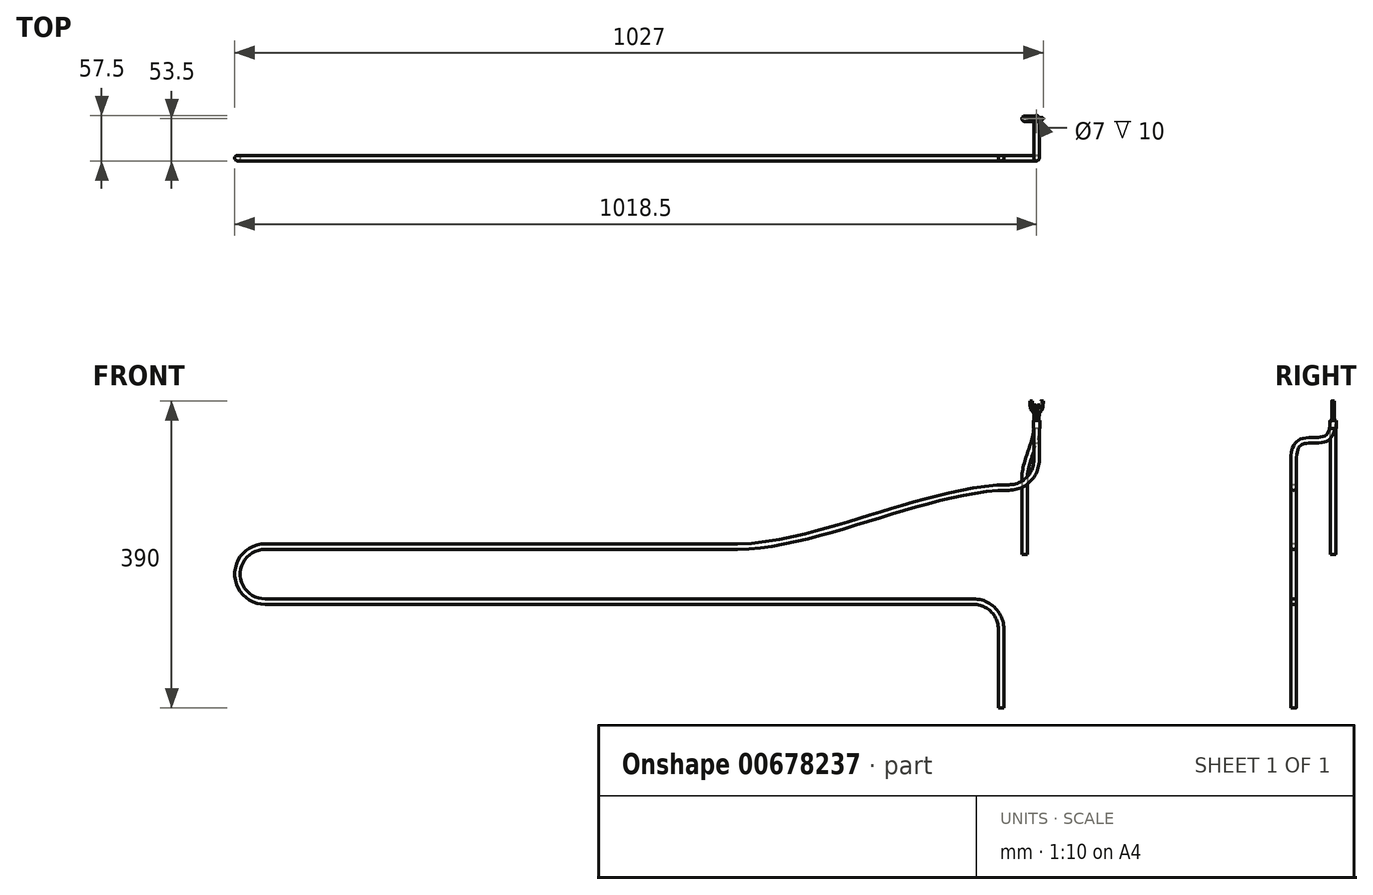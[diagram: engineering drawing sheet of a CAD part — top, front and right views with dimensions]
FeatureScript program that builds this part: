
annotation { "Feature Type Name" : "Feature", "Feature Type Description" : "" }
export const myFeature = defineFeature(function(context is Context, id is Id, definition is map)
    precondition{}
    {
        {
            var Q0;
            Q0=qCreatedBy(makeId("Top.planeOp"),FACE);
            var sketch = newSketch(context, id + "F0", { "sketchPlane" : qUnion([Q0])});
            skCircle(sketch, "E0", {"center": v(0, 0) * mm, "radius": 3.5 * mm});
            skSolve(sketch);
        }
        {
            var Q0;
            Q0=qCreatedBy(makeId("Front.planeOp"),FACE);
            var sketch = newSketch(context, id + "F1", { "sketchPlane" : qUnion([Q0])});
            skLineSegment(sketch, "E1", {"start": v(0, 0) * mm, "end": v(0, -10) * mm});
            skFitSpline(sketch, "E2", {"points": [v(0, -10) * mm, v(-15, -70) * mm], "startDerivative": vector(0, -45) * mm, "endDerivative": vector(0, -45) * mm});
            skLineSegment(sketch, "E3", {"start": v(-15, -70) * mm, "end": v(-15, -170) * mm});
            skSolve(sketch);
        }
        {
            var Q0;
            Q0=qSketchRegion(id+"F0",true);
            var Q1;
            Q1=qConstructionFilter(qBodyType(qCreatedBy(id+"F1",EDGE),BodyType.WIRE),ConstructionObject.NO);
            sweep(context, id + "F2", {"profiles" : qUnion([Q0]), "path" : qUnion([Q1])});
        }
        {
            var Q0;
            Q0=makeQuery(id+"F2.opSweep","CAP_FACE",FACE,{"disambiguationData":[OSD([sQuery(id+"F0.wireOp",EDGE,"E0"),sQuery(id+"F1.wireOp",VERTEX,"E1.start")])],"isStart":true});
            var sketch = newSketch(context, id + "F3", { "sketchPlane" : qUnion([Q0])});
            skCircle(sketch, "E4", {"center": v(1.5, 0) * mm, "radius": 1.5 * mm});
            skSolve(sketch);
        }
        {
            var Q0;
            Q0=qCreatedBy(makeId("Front.planeOp"),FACE);
            var sketch = newSketch(context, id + "F4", { "sketchPlane" : qUnion([Q0])});
            skFitSpline(sketch, "E5", {"points": [v(1.5, 0) * mm, v(2.5, 15) * mm], "startDerivative": vector(0, 15) * mm, "endDerivative": vector(0, 15) * mm});
            skLineSegment(sketch, "E6", {"start": v(2.5, 15) * mm, "end": v(2.5, 20) * mm});
            skSolve(sketch);
        }
        {
            var Q0;
            Q0=qSketchRegion(id+"F3",true);
            var Q1;
            Q1=qConstructionFilter(qBodyType(qCreatedBy(id+"F4",EDGE),BodyType.WIRE),ConstructionObject.NO);
            sweep(context, id + "F5", {"profiles" : qUnion([Q0]), "path" : qUnion([Q1])});
        }
        {
            var Q0;
            Q0=makeQuery(id+"F5.opSweep","SWEPT_BODY",BODY,{"disambiguationData":[OSD([sQuery(id+"F3.wireOp",EDGE,"E4"),sQuery(id+"F4.wireOp",EDGE,"E6")])]});
            var Q1;
            Q1=qCreatedBy(makeId("Right.planeOp"),FACE);
            mirror(context, id + "F6", {"entities" : qUnion([Q0]), "mirrorPlane" : qUnion([Q1])});
        }
        {
            var Q0;
            Q0=makeQuery(id+"F2.opSweep","CAP_FACE",FACE,{"disambiguationData":[OSD([sQuery(id+"F0.wireOp",EDGE,"E0"),sQuery(id+"F1.wireOp",VERTEX,"E1.start")])],"isStart":true});
            var sketch = newSketch(context, id + "F7", { "sketchPlane" : qUnion([Q0])});
            skCircle(sketch, "E7.0", {"center": v(0, 0) * mm, "radius": 3.5 * mm});
            skCircle(sketch, "E8.0", {"center": v(0, 0) * mm, "radius": 4 * mm});
            skSolve(sketch);
        }
        {
            var Q0;
            Q0=qSketchRegion(id+"F7",true);
            extrude(context, id + "F8", {"entities" : qUnion([Q0]), "oppositeDirection" : true, "depth" : 10 * mm, "offsetDistance" : 25 * mm});
        }
        {
            var Q0;
            Q0=qCreatedBy(makeId("Front.planeOp"),FACE);
            var sketch = newSketch(context, id + "F9", { "sketchPlane" : qUnion([Q0])});
            skFitSpline(sketch, "E9", {"points": [v(1.5, 0) * mm, v(4.25, 12.5) * mm, v(7, 25) * mm], "startDerivative": vector(0, 60) * mm, "endDerivative": vector(0, 60) * mm});
            skLineSegment(sketch, "E10", {"start": v(1.5, 10) * mm, "end": v(1.5, 0) * mm, "construction": true});
            skLineSegment(sketch, "E11", {"start": v(7, 25) * mm, "end": v(7, 15) * mm, "construction": true});
            skLineSegment(sketch, "E12", {"start": v(1.5, 0) * mm, "end": v(7, 25) * mm, "construction": true});
            skSolve(sketch);
        }
        {
            var Q0;
            Q0=qSketchRegion(id+"F3",true);
            var Q1;
            Q1=sQuery(id+"F9.wireOp",EDGE,"E9");
            sweep(context, id + "F10", {"profiles" : qUnion([Q0]), "path" : qUnion([Q1])});
        }
        {
            var Q0;
            Q0=makeQuery(id+"F10.opSweep","SWEPT_BODY",BODY,{"disambiguationData":[OSD([sQuery(id+"F3.wireOp",EDGE,"E4"),sQuery(id+"F9.wireOp",EDGE,"E9")])]});
            var Q1;
            Q1=qCreatedBy(makeId("Right.planeOp"),FACE);
            mirror(context, id + "F11", {"entities" : qUnion([Q0]), "mirrorPlane" : qUnion([Q1])});
        }
        {
            var Q0;
            Q0=qCreatedBy(makeId("Right.planeOp"),FACE);
            var sketch = newSketch(context, id + "F12", { "sketchPlane" : qUnion([Q0])});
            skFitSpline(sketch, "E13", {"points": [v(0, 0) * mm, v(-25, -25) * mm, v(-50, -50) * mm], "startDerivative": vector(0, -150) * mm, "endDerivative": vector(0, -150) * mm});
            skLineSegment(sketch, "E14", {"start": v(-50, -25) * mm, "end": v(-50, -50) * mm, "construction": true});
            skLineSegment(sketch, "E15", {"start": v(0, -25) * mm, "end": v(0, 0) * mm, "construction": true});
            skLineSegment(sketch, "E16", {"start": v(0, 0) * mm, "end": v(-50, -50) * mm, "construction": true});
            skSolve(sketch);
        }
        {
            var Q0;
            Q0=qCreatedBy(makeId("Front.planeOp"),FACE);
            var Q1;
            Q1=sQuery(id+"F12.wireOp",VERTEX,"E13.2.internal");
            cPlane(context, id + "F13", {"entities" : qUnion([Q0, Q1]), "cplaneType" : CPlaneType.PLANE_POINT, "offset" : 25 * mm, "width" : 150 * mm, "height" : 150 * mm});
        }
        {
            var Q0;
            Q0=qCreatedBy(id+"F13.planeOp",FACE);
            var sketch = newSketch(context, id + "F14", { "sketchPlane" : qUnion([Q0])});
            skLineSegment(sketch, "E17", {"start": v(-380, -160) * mm, "end": v(-980, -160) * mm});
            skArc(sketch, "E18", {"start": v(-980, -160) * mm, "mid": v(-1015, -195) * mm, "end": v(-980, -230) * mm});
            skLineSegment(sketch, "E19", {"start": v(-980, -230) * mm, "end": v(-80, -230) * mm});
            skArc(sketch, "E20", {"start": v(-45, -265) * mm, "mid": v(-55.25, -240.25) * mm, "end": v(-80, -230) * mm});
            skLineSegment(sketch, "E21", {"start": v(-45, -265) * mm, "end": v(-45, -365) * mm});
            skArc(sketch, "E22", {"start": v(-35, -85) * mm, "mid": v(-10.25, -74.75) * mm, "end": v(0, -50) * mm});
            skFitSpline(sketch, "E23", {"points": [v(-380, -160) * mm, v(-207.5, -122.5) * mm, v(-35, -85) * mm], "startDerivative": vector(300, 0) * mm, "endDerivative": vector(300, 0) * mm});
            skLineSegment(sketch, "E24", {"start": v(-85, -85) * mm, "end": v(-35, -85) * mm, "construction": true});
            skLineSegment(sketch, "E25", {"start": v(-330, -160) * mm, "end": v(-380, -160) * mm, "construction": true});
            skLineSegment(sketch, "E26", {"start": v(-380, -160) * mm, "end": v(-35, -85) * mm, "construction": true});
            skSolve(sketch);
        }
        {
            var Q0;
            Q0=qSketchRegion(id+"F0",true);
            var Q1;
            Q1=sQuery(id+"F12.wireOp",EDGE,"E13");
            var Q2;
            Q2=qConstructionFilter(qBodyType(qCreatedBy(id+"F14",EDGE),BodyType.WIRE),ConstructionObject.NO);
            sweep(context, id + "F15", {"profiles" : qUnion([Q0]), "path" : qUnion([Q1, Q2])});
        }
    });
